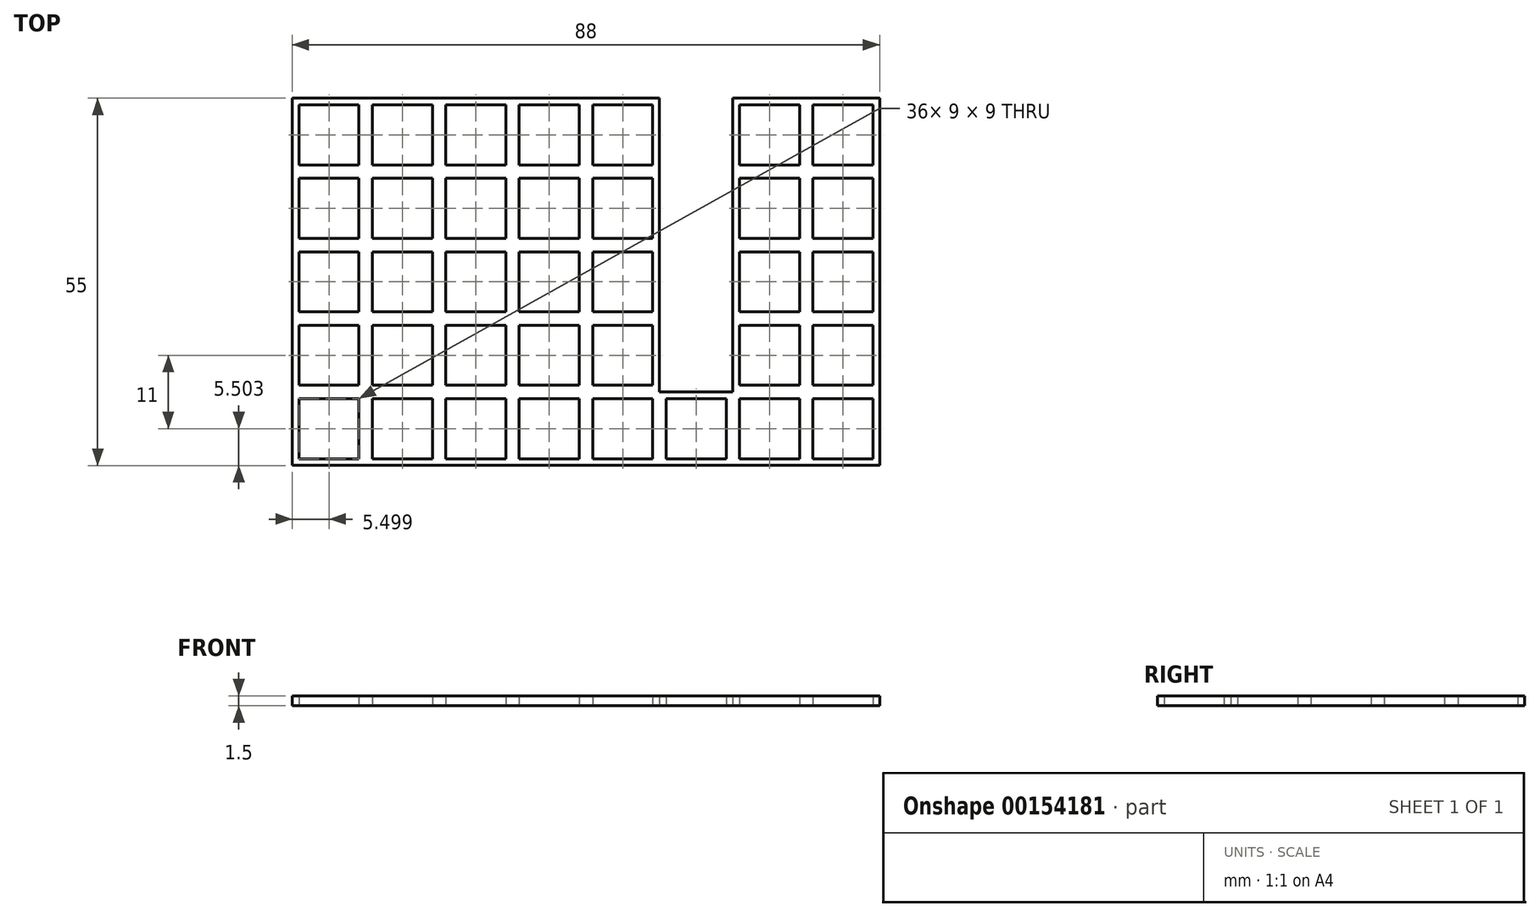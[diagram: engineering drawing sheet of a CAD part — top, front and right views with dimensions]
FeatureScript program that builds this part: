
annotation { "Feature Type Name" : "Feature", "Feature Type Description" : "" }
export const myFeature = defineFeature(function(context is Context, id is Id, definition is map)
    precondition{}
    {
        {
            var Q0;
            Q0=qCreatedBy(makeId("Top.planeOp"),FACE);
            var sketch = newSketch(context, id + "F0", { "sketchPlane" : qUnion([Q0])});
            skLineSegment(sketch, "E0.bottom", {"start": v(-68.25, 31) * mm, "end": v(19.75, 31) * mm, "construction": true});
            skLineSegment(sketch, "E0.top", {"start": v(-68.25, -24) * mm, "end": v(19.75, -24) * mm, "construction": true});
            skLineSegment(sketch, "E0.left", {"start": v(-68.25, 31) * mm, "end": v(-68.25, -24) * mm, "construction": true});
            skLineSegment(sketch, "E0.right", {"start": v(19.75, 31) * mm, "end": v(19.75, -24) * mm, "construction": true});
            skLineSegment(sketch, "E1.bottom", {"start": v(-68.25, -24) * mm, "end": v(-57.25, -24) * mm, "construction": true});
            skLineSegment(sketch, "E1.top", {"start": v(-68.25, -13) * mm, "end": v(-57.25, -13) * mm, "construction": true});
            skLineSegment(sketch, "E1.right", {"start": v(-57.25, -24) * mm, "end": v(-57.25, -13) * mm, "construction": true});
            skLineSegment(sketch, "E2.bottom", {"start": v(-68.25, -13) * mm, "end": v(-57.25, -13) * mm});
            skLineSegment(sketch, "E2.top", {"start": v(-68.25, -24) * mm, "end": v(-57.25, -24) * mm});
            skLineSegment(sketch, "E2.left", {"start": v(-68.25, -13) * mm, "end": v(-68.25, -24) * mm});
            skLineSegment(sketch, "E2.right", {"start": v(-57.25, -13) * mm, "end": v(-57.25, -24) * mm});
            skLineSegment(sketch, "E3", {"start": v(-67.25, -14) * mm, "end": v(-58.25, -14) * mm});
            skLineSegment(sketch, "E4", {"start": v(-58.25, -14) * mm, "end": v(-58.25, -23) * mm});
            skLineSegment(sketch, "E5", {"start": v(-58.25, -23) * mm, "end": v(-67.25, -23) * mm});
            skLineSegment(sketch, "E6", {"start": v(-67.25, -23) * mm, "end": v(-67.25, -14) * mm});
            skLineSegment(sketch, "E7.1.0.0", {"start": v(-47.25, -14) * mm, "end": v(-47.25, -23) * mm});
            skLineSegment(sketch, "E7.1.0.1", {"start": v(-57.25, -24) * mm, "end": v(-46.25, -24) * mm});
            skLineSegment(sketch, "E7.1.0.2", {"start": v(-56.25, -23) * mm, "end": v(-56.25, -14) * mm});
            skLineSegment(sketch, "E7.1.0.3", {"start": v(-56.25, -14) * mm, "end": v(-47.25, -14) * mm});
            skLineSegment(sketch, "E7.1.0.4", {"start": v(-46.25, -13) * mm, "end": v(-46.25, -24) * mm});
            skLineSegment(sketch, "E7.1.0.6", {"start": v(-57.25, -13) * mm, "end": v(-46.25, -13) * mm});
            skLineSegment(sketch, "E7.1.0.7", {"start": v(-47.25, -23) * mm, "end": v(-56.25, -23) * mm});
            skLineSegment(sketch, "E7.1.0.8", {"start": v(-57.25, -24) * mm, "end": v(-46.25, -24) * mm, "construction": true});
            skLineSegment(sketch, "E7.1.0.9", {"start": v(-46.25, -24) * mm, "end": v(-46.25, -13) * mm, "construction": true});
            skLineSegment(sketch, "E7.1.0.10", {"start": v(-57.25, -13) * mm, "end": v(-46.25, -13) * mm, "construction": true});
            skLineSegment(sketch, "E7.2.0.0", {"start": v(-36.25, -14) * mm, "end": v(-36.25, -23) * mm});
            skLineSegment(sketch, "E7.2.0.1", {"start": v(-46.25, -24) * mm, "end": v(-35.25, -24) * mm});
            skLineSegment(sketch, "E7.2.0.2", {"start": v(-45.25, -23) * mm, "end": v(-45.25, -14) * mm});
            skLineSegment(sketch, "E7.2.0.3", {"start": v(-45.25, -14) * mm, "end": v(-36.25, -14) * mm});
            skLineSegment(sketch, "E7.2.0.4", {"start": v(-35.25, -13) * mm, "end": v(-35.25, -24) * mm});
            skLineSegment(sketch, "E7.2.0.5", {"start": v(-46.25, -13) * mm, "end": v(-46.25, -24) * mm});
            skLineSegment(sketch, "E7.2.0.6", {"start": v(-46.25, -13) * mm, "end": v(-35.25, -13) * mm});
            skLineSegment(sketch, "E7.2.0.7", {"start": v(-36.25, -23) * mm, "end": v(-45.25, -23) * mm});
            skLineSegment(sketch, "E7.2.0.8", {"start": v(-46.25, -24) * mm, "end": v(-35.25, -24) * mm, "construction": true});
            skLineSegment(sketch, "E7.2.0.9", {"start": v(-35.25, -24) * mm, "end": v(-35.25, -13) * mm, "construction": true});
            skLineSegment(sketch, "E7.2.0.10", {"start": v(-46.25, -13) * mm, "end": v(-35.25, -13) * mm, "construction": true});
            skLineSegment(sketch, "E7.3.0.0", {"start": v(-25.25, -14) * mm, "end": v(-25.25, -23) * mm});
            skLineSegment(sketch, "E7.3.0.1", {"start": v(-35.25, -24) * mm, "end": v(-24.25, -24) * mm});
            skLineSegment(sketch, "E7.3.0.2", {"start": v(-34.25, -23) * mm, "end": v(-34.25, -14) * mm});
            skLineSegment(sketch, "E7.3.0.3", {"start": v(-34.25, -14) * mm, "end": v(-25.25, -14) * mm});
            skLineSegment(sketch, "E7.3.0.4", {"start": v(-24.25, -13) * mm, "end": v(-24.25, -24) * mm});
            skLineSegment(sketch, "E7.3.0.5", {"start": v(-35.25, -13) * mm, "end": v(-35.25, -24) * mm});
            skLineSegment(sketch, "E7.3.0.6", {"start": v(-35.25, -13) * mm, "end": v(-24.25, -13) * mm});
            skLineSegment(sketch, "E7.3.0.7", {"start": v(-25.25, -23) * mm, "end": v(-34.25, -23) * mm});
            skLineSegment(sketch, "E7.3.0.8", {"start": v(-35.25, -24) * mm, "end": v(-24.25, -24) * mm, "construction": true});
            skLineSegment(sketch, "E7.3.0.9", {"start": v(-24.25, -24) * mm, "end": v(-24.25, -13) * mm, "construction": true});
            skLineSegment(sketch, "E7.3.0.10", {"start": v(-35.25, -13) * mm, "end": v(-24.25, -13) * mm, "construction": true});
            skLineSegment(sketch, "E7.4.0.0", {"start": v(-14.25, -14) * mm, "end": v(-14.25, -23) * mm});
            skLineSegment(sketch, "E7.4.0.1", {"start": v(-24.25, -24) * mm, "end": v(-13.25, -24) * mm});
            skLineSegment(sketch, "E7.4.0.2", {"start": v(-23.25, -23) * mm, "end": v(-23.25, -14) * mm});
            skLineSegment(sketch, "E7.4.0.3", {"start": v(-23.25, -14) * mm, "end": v(-14.25, -14) * mm});
            skLineSegment(sketch, "E7.4.0.4", {"start": v(-13.25, -13) * mm, "end": v(-13.25, -24) * mm});
            skLineSegment(sketch, "E7.4.0.5", {"start": v(-24.25, -13) * mm, "end": v(-24.25, -24) * mm});
            skLineSegment(sketch, "E7.4.0.6", {"start": v(-24.25, -13) * mm, "end": v(-13.25, -13) * mm});
            skLineSegment(sketch, "E7.4.0.7", {"start": v(-14.25, -23) * mm, "end": v(-23.25, -23) * mm});
            skLineSegment(sketch, "E7.4.0.8", {"start": v(-24.25, -24) * mm, "end": v(-13.25, -24) * mm, "construction": true});
            skLineSegment(sketch, "E7.4.0.9", {"start": v(-13.25, -24) * mm, "end": v(-13.25, -13) * mm, "construction": true});
            skLineSegment(sketch, "E7.4.0.10", {"start": v(-24.25, -13) * mm, "end": v(-13.25, -13) * mm, "construction": true});
            skLineSegment(sketch, "E7.5.0.0", {"start": v(-3.25, -14) * mm, "end": v(-3.25, -23) * mm});
            skLineSegment(sketch, "E7.5.0.1", {"start": v(-13.25, -24) * mm, "end": v(-2.25, -24) * mm});
            skLineSegment(sketch, "E7.5.0.2", {"start": v(-12.25, -23) * mm, "end": v(-12.25, -14) * mm});
            skLineSegment(sketch, "E7.5.0.3", {"start": v(-12.25, -14) * mm, "end": v(-3.25, -14) * mm});
            skLineSegment(sketch, "E7.5.0.4", {"start": v(-2.25, -13) * mm, "end": v(-2.25, -24) * mm});
            skLineSegment(sketch, "E7.5.0.5", {"start": v(-13.25, -13) * mm, "end": v(-13.25, -24) * mm});
            skLineSegment(sketch, "E7.5.0.6", {"start": v(-13.25, -13) * mm, "end": v(-2.25, -13) * mm});
            skLineSegment(sketch, "E7.5.0.7", {"start": v(-3.25, -23) * mm, "end": v(-12.25, -23) * mm});
            skLineSegment(sketch, "E7.5.0.8", {"start": v(-13.25, -24) * mm, "end": v(-2.25, -24) * mm, "construction": true});
            skLineSegment(sketch, "E7.5.0.9", {"start": v(-2.25, -24) * mm, "end": v(-2.25, -13) * mm, "construction": true});
            skLineSegment(sketch, "E7.5.0.10", {"start": v(-13.25, -13) * mm, "end": v(-2.25, -13) * mm, "construction": true});
            skLineSegment(sketch, "E7.6.0.0", {"start": v(7.75, -14) * mm, "end": v(7.75, -23) * mm});
            skLineSegment(sketch, "E7.6.0.1", {"start": v(-2.25, -24) * mm, "end": v(8.75, -24) * mm});
            skLineSegment(sketch, "E7.6.0.2", {"start": v(-1.25, -23) * mm, "end": v(-1.25, -14) * mm});
            skLineSegment(sketch, "E7.6.0.3", {"start": v(-1.25, -14) * mm, "end": v(7.75, -14) * mm});
            skLineSegment(sketch, "E7.6.0.4", {"start": v(8.75, -13) * mm, "end": v(8.75, -24) * mm});
            skLineSegment(sketch, "E7.6.0.5", {"start": v(-2.25, -13) * mm, "end": v(-2.25, -24) * mm});
            skLineSegment(sketch, "E7.6.0.6", {"start": v(-2.25, -13) * mm, "end": v(8.75, -13) * mm});
            skLineSegment(sketch, "E7.6.0.7", {"start": v(7.75, -23) * mm, "end": v(-1.25, -23) * mm});
            skLineSegment(sketch, "E7.6.0.8", {"start": v(-2.25, -24) * mm, "end": v(8.75, -24) * mm, "construction": true});
            skLineSegment(sketch, "E7.6.0.9", {"start": v(8.75, -24) * mm, "end": v(8.75, -13) * mm, "construction": true});
            skLineSegment(sketch, "E7.6.0.10", {"start": v(-2.25, -13) * mm, "end": v(8.75, -13) * mm, "construction": true});
            skLineSegment(sketch, "E7.7.0.0", {"start": v(18.75, -14) * mm, "end": v(18.75, -23) * mm});
            skLineSegment(sketch, "E7.7.0.1", {"start": v(8.75, -24) * mm, "end": v(19.75, -24) * mm});
            skLineSegment(sketch, "E7.7.0.2", {"start": v(9.75, -23) * mm, "end": v(9.75, -14) * mm});
            skLineSegment(sketch, "E7.7.0.3", {"start": v(9.75, -14) * mm, "end": v(18.75, -14) * mm});
            skLineSegment(sketch, "E7.7.0.4", {"start": v(19.75, -13) * mm, "end": v(19.75, -24) * mm});
            skLineSegment(sketch, "E7.7.0.5", {"start": v(8.75, -13) * mm, "end": v(8.75, -24) * mm});
            skLineSegment(sketch, "E7.7.0.6", {"start": v(8.75, -13) * mm, "end": v(19.75, -13) * mm});
            skLineSegment(sketch, "E7.7.0.7", {"start": v(18.75, -23) * mm, "end": v(9.75, -23) * mm});
            skLineSegment(sketch, "E7.7.0.8", {"start": v(8.75, -24) * mm, "end": v(19.75, -24) * mm, "construction": true});
            skLineSegment(sketch, "E7.7.0.9", {"start": v(19.75, -24) * mm, "end": v(19.75, -13) * mm, "construction": true});
            skLineSegment(sketch, "E7.7.0.10", {"start": v(8.75, -13) * mm, "end": v(19.75, -13) * mm, "construction": true});
            skLineSegment(sketch, "E8.0.1.0", {"start": v(-56.25, -12) * mm, "end": v(-56.25, -3) * mm});
            skLineSegment(sketch, "E8.0.1.1", {"start": v(-46.25, -2) * mm, "end": v(-35.25, -2) * mm});
            skLineSegment(sketch, "E8.0.1.2", {"start": v(-14.25, -3) * mm, "end": v(-14.25, -12) * mm});
            skLineSegment(sketch, "E8.0.1.3", {"start": v(-13.25, -2) * mm, "end": v(-13.25, -13) * mm});
            skLineSegment(sketch, "E8.0.1.5", {"start": v(-2.25, -2) * mm, "end": v(8.75, -2) * mm});
            skLineSegment(sketch, "E8.0.1.6", {"start": v(-45.25, -12) * mm, "end": v(-45.25, -3) * mm});
            skLineSegment(sketch, "E8.0.1.7", {"start": v(-25.25, -12) * mm, "end": v(-34.25, -12) * mm});
            skLineSegment(sketch, "E8.0.1.9", {"start": v(-45.25, -3) * mm, "end": v(-36.25, -3) * mm});
            skLineSegment(sketch, "E8.0.1.10", {"start": v(-58.25, -3) * mm, "end": v(-58.25, -12) * mm});
            skLineSegment(sketch, "E8.0.1.11", {"start": v(-12.25, -12) * mm, "end": v(-12.25, -3) * mm});
            skLineSegment(sketch, "E8.0.1.12", {"start": v(-67.25, -3) * mm, "end": v(-58.25, -3) * mm});
            skLineSegment(sketch, "E8.0.1.13", {"start": v(-57.25, -2) * mm, "end": v(-57.25, -13) * mm});
            skLineSegment(sketch, "E8.0.1.14", {"start": v(-68.25, -2) * mm, "end": v(-68.25, -13) * mm});
            skLineSegment(sketch, "E8.0.1.16", {"start": v(7.75, -12) * mm, "end": v(-1.25, -12) * mm});
            skLineSegment(sketch, "E8.0.1.18", {"start": v(-35.25, -2) * mm, "end": v(-24.25, -2) * mm});
            skLineSegment(sketch, "E8.0.1.19", {"start": v(-3.25, -3) * mm, "end": v(-3.25, -12) * mm});
            skLineSegment(sketch, "E8.0.1.20", {"start": v(8.75, -2) * mm, "end": v(8.75, -13) * mm});
            skLineSegment(sketch, "E8.0.1.21", {"start": v(-36.25, -3) * mm, "end": v(-36.25, -12) * mm});
            skLineSegment(sketch, "E8.0.1.22", {"start": v(-68.25, -2) * mm, "end": v(-57.25, -2) * mm});
            skLineSegment(sketch, "E8.0.1.23", {"start": v(-47.25, -3) * mm, "end": v(-47.25, -12) * mm});
            skLineSegment(sketch, "E8.0.1.24", {"start": v(-67.25, -12) * mm, "end": v(-67.25, -3) * mm});
            skLineSegment(sketch, "E8.0.1.25", {"start": v(-58.25, -12) * mm, "end": v(-67.25, -12) * mm});
            skLineSegment(sketch, "E8.0.1.26", {"start": v(-46.25, -2) * mm, "end": v(-46.25, -13) * mm});
            skLineSegment(sketch, "E8.0.1.27", {"start": v(-2.25, -2) * mm, "end": v(-2.25, -13) * mm});
            skLineSegment(sketch, "E8.0.1.28", {"start": v(-1.25, -3) * mm, "end": v(7.75, -3) * mm});
            skLineSegment(sketch, "E8.0.1.29", {"start": v(-24.25, -2) * mm, "end": v(-24.25, -13) * mm});
            skLineSegment(sketch, "E8.0.1.30", {"start": v(-35.25, -2) * mm, "end": v(-35.25, -13) * mm});
            skLineSegment(sketch, "E8.0.1.31", {"start": v(-12.25, -3) * mm, "end": v(-3.25, -3) * mm});
            skLineSegment(sketch, "E8.0.1.32", {"start": v(-1.25, -12) * mm, "end": v(-1.25, -3) * mm});
            skLineSegment(sketch, "E8.0.1.33", {"start": v(18.75, -12) * mm, "end": v(9.75, -12) * mm});
            skLineSegment(sketch, "E8.0.1.34", {"start": v(-34.25, -3) * mm, "end": v(-25.25, -3) * mm});
            skLineSegment(sketch, "E8.0.1.35", {"start": v(18.75, -3) * mm, "end": v(18.75, -12) * mm});
            skLineSegment(sketch, "E8.0.1.36", {"start": v(-13.25, -2) * mm, "end": v(-2.25, -2) * mm});
            skLineSegment(sketch, "E8.0.1.38", {"start": v(-36.25, -12) * mm, "end": v(-45.25, -12) * mm});
            skLineSegment(sketch, "E8.0.1.40", {"start": v(8.75, -2) * mm, "end": v(19.75, -2) * mm});
            skLineSegment(sketch, "E8.0.1.41", {"start": v(-56.25, -3) * mm, "end": v(-47.25, -3) * mm});
            skLineSegment(sketch, "E8.0.1.43", {"start": v(-34.25, -12) * mm, "end": v(-34.25, -3) * mm});
            skLineSegment(sketch, "E8.0.1.44", {"start": v(-14.25, -12) * mm, "end": v(-23.25, -12) * mm});
            skLineSegment(sketch, "E8.0.1.45", {"start": v(-57.25, -2) * mm, "end": v(-46.25, -2) * mm});
            skLineSegment(sketch, "E8.0.1.46", {"start": v(19.75, -2) * mm, "end": v(19.75, -13) * mm});
            skLineSegment(sketch, "E8.0.1.47", {"start": v(-25.25, -3) * mm, "end": v(-25.25, -12) * mm});
            skLineSegment(sketch, "E8.0.1.48", {"start": v(-47.25, -12) * mm, "end": v(-56.25, -12) * mm});
            skLineSegment(sketch, "E8.0.1.49", {"start": v(7.75, -3) * mm, "end": v(7.75, -12) * mm});
            skLineSegment(sketch, "E8.0.1.50", {"start": v(-24.25, -2) * mm, "end": v(-13.25, -2) * mm});
            skLineSegment(sketch, "E8.0.1.52", {"start": v(-23.25, -12) * mm, "end": v(-23.25, -3) * mm});
            skLineSegment(sketch, "E8.0.1.53", {"start": v(-3.25, -12) * mm, "end": v(-12.25, -12) * mm});
            skLineSegment(sketch, "E8.0.1.54", {"start": v(9.75, -12) * mm, "end": v(9.75, -3) * mm});
            skLineSegment(sketch, "E8.0.1.55", {"start": v(9.75, -3) * mm, "end": v(18.75, -3) * mm});
            skLineSegment(sketch, "E8.0.1.56", {"start": v(-23.25, -3) * mm, "end": v(-14.25, -3) * mm});
            skLineSegment(sketch, "E8.0.1.57", {"start": v(-2.25, -2) * mm, "end": v(8.75, -2) * mm, "construction": true});
            skLineSegment(sketch, "E8.0.1.58", {"start": v(-2.25, -2) * mm, "end": v(-2.25, -13) * mm});
            skLineSegment(sketch, "E8.0.1.59", {"start": v(8.75, -2) * mm, "end": v(19.75, -2) * mm, "construction": true});
            skLineSegment(sketch, "E8.0.1.60", {"start": v(19.75, -13) * mm, "end": v(19.75, -2) * mm, "construction": true});
            skLineSegment(sketch, "E8.0.1.61", {"start": v(-35.25, -2) * mm, "end": v(-35.25, -13) * mm});
            skLineSegment(sketch, "E8.0.1.62", {"start": v(-24.25, -2) * mm, "end": v(-13.25, -2) * mm, "construction": true});
            skLineSegment(sketch, "E8.0.1.63", {"start": v(-68.25, -2) * mm, "end": v(-57.25, -2) * mm, "construction": true});
            skLineSegment(sketch, "E8.0.1.65", {"start": v(-68.25, -13) * mm, "end": v(19.75, -13) * mm, "construction": true});
            skLineSegment(sketch, "E8.0.1.66", {"start": v(-35.25, -2) * mm, "end": v(-24.25, -2) * mm, "construction": true});
            skLineSegment(sketch, "E8.0.1.67", {"start": v(-57.25, -2) * mm, "end": v(-46.25, -2) * mm, "construction": true});
            skLineSegment(sketch, "E8.0.1.68", {"start": v(-13.25, -2) * mm, "end": v(-13.25, -13) * mm});
            skLineSegment(sketch, "E8.0.1.69", {"start": v(-46.25, -2) * mm, "end": v(-35.25, -2) * mm, "construction": true});
            skLineSegment(sketch, "E8.0.1.70", {"start": v(-13.25, -2) * mm, "end": v(-2.25, -2) * mm, "construction": true});
            skLineSegment(sketch, "E8.0.1.71", {"start": v(-24.25, -2) * mm, "end": v(-24.25, -13) * mm});
            skLineSegment(sketch, "E8.0.1.72", {"start": v(8.75, -2) * mm, "end": v(8.75, -13) * mm});
            skLineSegment(sketch, "E8.0.1.74", {"start": v(-46.25, -2) * mm, "end": v(-46.25, -13) * mm});
            skLineSegment(sketch, "E8.0.1.75", {"start": v(-57.25, -2) * mm, "end": v(-57.25, -13) * mm});
            skLineSegment(sketch, "E8.0.1.79", {"start": v(-57.25, -13) * mm, "end": v(-57.25, -2) * mm, "construction": true});
            skLineSegment(sketch, "E8.0.1.80", {"start": v(8.75, -13) * mm, "end": v(8.75, -2) * mm, "construction": true});
            skLineSegment(sketch, "E8.0.1.82", {"start": v(-13.25, -13) * mm, "end": v(-13.25, -2) * mm, "construction": true});
            skLineSegment(sketch, "E8.0.1.83", {"start": v(-24.25, -13) * mm, "end": v(-24.25, -2) * mm, "construction": true});
            skLineSegment(sketch, "E8.0.1.84", {"start": v(-46.25, -13) * mm, "end": v(-46.25, -2) * mm, "construction": true});
            skLineSegment(sketch, "E8.0.1.88", {"start": v(-2.25, -13) * mm, "end": v(-2.25, -2) * mm, "construction": true});
            skLineSegment(sketch, "E8.0.1.89", {"start": v(-35.25, -13) * mm, "end": v(-35.25, -2) * mm, "construction": true});
            skLineSegment(sketch, "E8.0.2.0", {"start": v(-56.25, -1) * mm, "end": v(-56.25, 8) * mm});
            skLineSegment(sketch, "E8.0.2.1", {"start": v(-46.25, 9) * mm, "end": v(-35.25, 9) * mm});
            skLineSegment(sketch, "E8.0.2.2", {"start": v(-14.25, 8) * mm, "end": v(-14.25, -1) * mm});
            skLineSegment(sketch, "E8.0.2.3", {"start": v(-13.25, 9) * mm, "end": v(-13.25, -2) * mm});
            skLineSegment(sketch, "E8.0.2.4", {"start": v(-57.25, -2) * mm, "end": v(-46.25, -2) * mm});
            skLineSegment(sketch, "E8.0.2.5", {"start": v(-2.25, 9) * mm, "end": v(8.75, 9) * mm});
            skLineSegment(sketch, "E8.0.2.6", {"start": v(-45.25, -1) * mm, "end": v(-45.25, 8) * mm});
            skLineSegment(sketch, "E8.0.2.7", {"start": v(-25.25, -1) * mm, "end": v(-34.25, -1) * mm});
            skLineSegment(sketch, "E8.0.2.8", {"start": v(-13.25, -2) * mm, "end": v(-2.25, -2) * mm});
            skLineSegment(sketch, "E8.0.2.9", {"start": v(-45.25, 8) * mm, "end": v(-36.25, 8) * mm});
            skLineSegment(sketch, "E8.0.2.10", {"start": v(-58.25, 8) * mm, "end": v(-58.25, -1) * mm});
            skLineSegment(sketch, "E8.0.2.11", {"start": v(-12.25, -1) * mm, "end": v(-12.25, 8) * mm});
            skLineSegment(sketch, "E8.0.2.12", {"start": v(-67.25, 8) * mm, "end": v(-58.25, 8) * mm});
            skLineSegment(sketch, "E8.0.2.13", {"start": v(-57.25, 9) * mm, "end": v(-57.25, -2) * mm});
            skLineSegment(sketch, "E8.0.2.14", {"start": v(-68.25, 9) * mm, "end": v(-68.25, -2) * mm});
            skLineSegment(sketch, "E8.0.2.15", {"start": v(-68.25, -2) * mm, "end": v(-57.25, -2) * mm});
            skLineSegment(sketch, "E8.0.2.16", {"start": v(7.75, -1) * mm, "end": v(-1.25, -1) * mm});
            skLineSegment(sketch, "E8.0.2.17", {"start": v(-46.25, -2) * mm, "end": v(-35.25, -2) * mm});
            skLineSegment(sketch, "E8.0.2.18", {"start": v(-35.25, 9) * mm, "end": v(-24.25, 9) * mm});
            skLineSegment(sketch, "E8.0.2.19", {"start": v(-3.25, 8) * mm, "end": v(-3.25, -1) * mm});
            skLineSegment(sketch, "E8.0.2.20", {"start": v(8.75, 9) * mm, "end": v(8.75, -2) * mm});
            skLineSegment(sketch, "E8.0.2.21", {"start": v(-36.25, 8) * mm, "end": v(-36.25, -1) * mm});
            skLineSegment(sketch, "E8.0.2.22", {"start": v(-68.25, 9) * mm, "end": v(-57.25, 9) * mm});
            skLineSegment(sketch, "E8.0.2.23", {"start": v(-47.25, 8) * mm, "end": v(-47.25, -1) * mm});
            skLineSegment(sketch, "E8.0.2.24", {"start": v(-67.25, -1) * mm, "end": v(-67.25, 8) * mm});
            skLineSegment(sketch, "E8.0.2.25", {"start": v(-58.25, -1) * mm, "end": v(-67.25, -1) * mm});
            skLineSegment(sketch, "E8.0.2.26", {"start": v(-46.25, 9) * mm, "end": v(-46.25, -2) * mm});
            skLineSegment(sketch, "E8.0.2.27", {"start": v(-2.25, 9) * mm, "end": v(-2.25, -2) * mm});
            skLineSegment(sketch, "E8.0.2.28", {"start": v(-1.25, 8) * mm, "end": v(7.75, 8) * mm});
            skLineSegment(sketch, "E8.0.2.29", {"start": v(-24.25, 9) * mm, "end": v(-24.25, -2) * mm});
            skLineSegment(sketch, "E8.0.2.30", {"start": v(-35.25, 9) * mm, "end": v(-35.25, -2) * mm});
            skLineSegment(sketch, "E8.0.2.31", {"start": v(-12.25, 8) * mm, "end": v(-3.25, 8) * mm});
            skLineSegment(sketch, "E8.0.2.32", {"start": v(-1.25, -1) * mm, "end": v(-1.25, 8) * mm});
            skLineSegment(sketch, "E8.0.2.33", {"start": v(18.75, -1) * mm, "end": v(9.75, -1) * mm});
            skLineSegment(sketch, "E8.0.2.34", {"start": v(-34.25, 8) * mm, "end": v(-25.25, 8) * mm});
            skLineSegment(sketch, "E8.0.2.35", {"start": v(18.75, 8) * mm, "end": v(18.75, -1) * mm});
            skLineSegment(sketch, "E8.0.2.36", {"start": v(-13.25, 9) * mm, "end": v(-2.25, 9) * mm});
            skLineSegment(sketch, "E8.0.2.37", {"start": v(-24.25, -2) * mm, "end": v(-13.25, -2) * mm});
            skLineSegment(sketch, "E8.0.2.38", {"start": v(-36.25, -1) * mm, "end": v(-45.25, -1) * mm});
            skLineSegment(sketch, "E8.0.2.39", {"start": v(-2.25, -2) * mm, "end": v(8.75, -2) * mm});
            skLineSegment(sketch, "E8.0.2.40", {"start": v(8.75, 9) * mm, "end": v(19.75, 9) * mm});
            skLineSegment(sketch, "E8.0.2.41", {"start": v(-56.25, 8) * mm, "end": v(-47.25, 8) * mm});
            skLineSegment(sketch, "E8.0.2.42", {"start": v(8.75, -2) * mm, "end": v(19.75, -2) * mm});
            skLineSegment(sketch, "E8.0.2.43", {"start": v(-34.25, -1) * mm, "end": v(-34.25, 8) * mm});
            skLineSegment(sketch, "E8.0.2.44", {"start": v(-14.25, -1) * mm, "end": v(-23.25, -1) * mm});
            skLineSegment(sketch, "E8.0.2.45", {"start": v(-57.25, 9) * mm, "end": v(-46.25, 9) * mm});
            skLineSegment(sketch, "E8.0.2.46", {"start": v(19.75, 9) * mm, "end": v(19.75, -2) * mm});
            skLineSegment(sketch, "E8.0.2.47", {"start": v(-25.25, 8) * mm, "end": v(-25.25, -1) * mm});
            skLineSegment(sketch, "E8.0.2.48", {"start": v(-47.25, -1) * mm, "end": v(-56.25, -1) * mm});
            skLineSegment(sketch, "E8.0.2.49", {"start": v(7.75, 8) * mm, "end": v(7.75, -1) * mm});
            skLineSegment(sketch, "E8.0.2.50", {"start": v(-24.25, 9) * mm, "end": v(-13.25, 9) * mm});
            skLineSegment(sketch, "E8.0.2.51", {"start": v(-35.25, -2) * mm, "end": v(-24.25, -2) * mm});
            skLineSegment(sketch, "E8.0.2.52", {"start": v(-23.25, -1) * mm, "end": v(-23.25, 8) * mm});
            skLineSegment(sketch, "E8.0.2.53", {"start": v(-3.25, -1) * mm, "end": v(-12.25, -1) * mm});
            skLineSegment(sketch, "E8.0.2.54", {"start": v(9.75, -1) * mm, "end": v(9.75, 8) * mm});
            skLineSegment(sketch, "E8.0.2.55", {"start": v(9.75, 8) * mm, "end": v(18.75, 8) * mm});
            skLineSegment(sketch, "E8.0.2.56", {"start": v(-23.25, 8) * mm, "end": v(-14.25, 8) * mm});
            skLineSegment(sketch, "E8.0.2.57", {"start": v(-2.25, 9) * mm, "end": v(8.75, 9) * mm, "construction": true});
            skLineSegment(sketch, "E8.0.2.58", {"start": v(-2.25, 9) * mm, "end": v(-2.25, -2) * mm});
            skLineSegment(sketch, "E8.0.2.59", {"start": v(8.75, 9) * mm, "end": v(19.75, 9) * mm, "construction": true});
            skLineSegment(sketch, "E8.0.2.60", {"start": v(19.75, -2) * mm, "end": v(19.75, 9) * mm, "construction": true});
            skLineSegment(sketch, "E8.0.2.61", {"start": v(-35.25, 9) * mm, "end": v(-35.25, -2) * mm});
            skLineSegment(sketch, "E8.0.2.62", {"start": v(-24.25, 9) * mm, "end": v(-13.25, 9) * mm, "construction": true});
            skLineSegment(sketch, "E8.0.2.63", {"start": v(-68.25, 9) * mm, "end": v(-57.25, 9) * mm, "construction": true});
            skLineSegment(sketch, "E8.0.2.64", {"start": v(-68.25, -2) * mm, "end": v(-57.25, -2) * mm, "construction": true});
            skLineSegment(sketch, "E8.0.2.65", {"start": v(-68.25, -2) * mm, "end": v(19.75, -2) * mm, "construction": true});
            skLineSegment(sketch, "E8.0.2.66", {"start": v(-35.25, 9) * mm, "end": v(-24.25, 9) * mm, "construction": true});
            skLineSegment(sketch, "E8.0.2.67", {"start": v(-57.25, 9) * mm, "end": v(-46.25, 9) * mm, "construction": true});
            skLineSegment(sketch, "E8.0.2.68", {"start": v(-13.25, 9) * mm, "end": v(-13.25, -2) * mm});
            skLineSegment(sketch, "E8.0.2.69", {"start": v(-46.25, 9) * mm, "end": v(-35.25, 9) * mm, "construction": true});
            skLineSegment(sketch, "E8.0.2.70", {"start": v(-13.25, 9) * mm, "end": v(-2.25, 9) * mm, "construction": true});
            skLineSegment(sketch, "E8.0.2.71", {"start": v(-24.25, 9) * mm, "end": v(-24.25, -2) * mm});
            skLineSegment(sketch, "E8.0.2.72", {"start": v(8.75, 9) * mm, "end": v(8.75, -2) * mm});
            skLineSegment(sketch, "E8.0.2.73", {"start": v(-46.25, -2) * mm, "end": v(-35.25, -2) * mm, "construction": true});
            skLineSegment(sketch, "E8.0.2.74", {"start": v(-46.25, 9) * mm, "end": v(-46.25, -2) * mm});
            skLineSegment(sketch, "E8.0.2.75", {"start": v(-57.25, 9) * mm, "end": v(-57.25, -2) * mm});
            skLineSegment(sketch, "E8.0.2.76", {"start": v(-2.25, -2) * mm, "end": v(8.75, -2) * mm, "construction": true});
            skLineSegment(sketch, "E8.0.2.77", {"start": v(-68.25, -2) * mm, "end": v(-57.25, -2) * mm, "construction": true});
            skLineSegment(sketch, "E8.0.2.78", {"start": v(-35.25, -2) * mm, "end": v(-24.25, -2) * mm, "construction": true});
            skLineSegment(sketch, "E8.0.2.79", {"start": v(-57.25, -2) * mm, "end": v(-57.25, 9) * mm, "construction": true});
            skLineSegment(sketch, "E8.0.2.80", {"start": v(8.75, -2) * mm, "end": v(8.75, 9) * mm, "construction": true});
            skLineSegment(sketch, "E8.0.2.81", {"start": v(8.75, -2) * mm, "end": v(19.75, -2) * mm, "construction": true});
            skLineSegment(sketch, "E8.0.2.82", {"start": v(-13.25, -2) * mm, "end": v(-13.25, 9) * mm, "construction": true});
            skLineSegment(sketch, "E8.0.2.83", {"start": v(-24.25, -2) * mm, "end": v(-24.25, 9) * mm, "construction": true});
            skLineSegment(sketch, "E8.0.2.84", {"start": v(-46.25, -2) * mm, "end": v(-46.25, 9) * mm, "construction": true});
            skLineSegment(sketch, "E8.0.2.85", {"start": v(-24.25, -2) * mm, "end": v(-13.25, -2) * mm, "construction": true});
            skLineSegment(sketch, "E8.0.2.86", {"start": v(-57.25, -2) * mm, "end": v(-46.25, -2) * mm, "construction": true});
            skLineSegment(sketch, "E8.0.2.87", {"start": v(-13.25, -2) * mm, "end": v(-2.25, -2) * mm, "construction": true});
            skLineSegment(sketch, "E8.0.2.88", {"start": v(-2.25, -2) * mm, "end": v(-2.25, 9) * mm, "construction": true});
            skLineSegment(sketch, "E8.0.2.89", {"start": v(-35.25, -2) * mm, "end": v(-35.25, 9) * mm, "construction": true});
            skLineSegment(sketch, "E8.0.3.0", {"start": v(-56.25, 10) * mm, "end": v(-56.25, 19) * mm});
            skLineSegment(sketch, "E8.0.3.1", {"start": v(-46.25, 20) * mm, "end": v(-35.25, 20) * mm});
            skLineSegment(sketch, "E8.0.3.2", {"start": v(-14.25, 19) * mm, "end": v(-14.25, 10) * mm});
            skLineSegment(sketch, "E8.0.3.3", {"start": v(-13.25, 20) * mm, "end": v(-13.25, 9) * mm});
            skLineSegment(sketch, "E8.0.3.4", {"start": v(-57.25, 9) * mm, "end": v(-46.25, 9) * mm});
            skLineSegment(sketch, "E8.0.3.5", {"start": v(-2.25, 20) * mm, "end": v(8.75, 20) * mm});
            skLineSegment(sketch, "E8.0.3.6", {"start": v(-45.25, 10) * mm, "end": v(-45.25, 19) * mm});
            skLineSegment(sketch, "E8.0.3.7", {"start": v(-25.25, 10) * mm, "end": v(-34.25, 10) * mm});
            skLineSegment(sketch, "E8.0.3.8", {"start": v(-13.25, 9) * mm, "end": v(-2.25, 9) * mm});
            skLineSegment(sketch, "E8.0.3.9", {"start": v(-45.25, 19) * mm, "end": v(-36.25, 19) * mm});
            skLineSegment(sketch, "E8.0.3.10", {"start": v(-58.25, 19) * mm, "end": v(-58.25, 10) * mm});
            skLineSegment(sketch, "E8.0.3.11", {"start": v(-12.25, 10) * mm, "end": v(-12.25, 19) * mm});
            skLineSegment(sketch, "E8.0.3.12", {"start": v(-67.25, 19) * mm, "end": v(-58.25, 19) * mm});
            skLineSegment(sketch, "E8.0.3.13", {"start": v(-57.25, 20) * mm, "end": v(-57.25, 9) * mm});
            skLineSegment(sketch, "E8.0.3.14", {"start": v(-68.25, 20) * mm, "end": v(-68.25, 9) * mm});
            skLineSegment(sketch, "E8.0.3.15", {"start": v(-68.25, 9) * mm, "end": v(-57.25, 9) * mm});
            skLineSegment(sketch, "E8.0.3.16", {"start": v(7.75, 10) * mm, "end": v(-1.25, 10) * mm});
            skLineSegment(sketch, "E8.0.3.17", {"start": v(-46.25, 9) * mm, "end": v(-35.25, 9) * mm});
            skLineSegment(sketch, "E8.0.3.18", {"start": v(-35.25, 20) * mm, "end": v(-24.25, 20) * mm});
            skLineSegment(sketch, "E8.0.3.19", {"start": v(-3.25, 19) * mm, "end": v(-3.25, 10) * mm});
            skLineSegment(sketch, "E8.0.3.20", {"start": v(8.75, 20) * mm, "end": v(8.75, 9) * mm});
            skLineSegment(sketch, "E8.0.3.21", {"start": v(-36.25, 19) * mm, "end": v(-36.25, 10) * mm});
            skLineSegment(sketch, "E8.0.3.22", {"start": v(-68.25, 20) * mm, "end": v(-57.25, 20) * mm});
            skLineSegment(sketch, "E8.0.3.23", {"start": v(-47.25, 19) * mm, "end": v(-47.25, 10) * mm});
            skLineSegment(sketch, "E8.0.3.24", {"start": v(-67.25, 10) * mm, "end": v(-67.25, 19) * mm});
            skLineSegment(sketch, "E8.0.3.25", {"start": v(-58.25, 10) * mm, "end": v(-67.25, 10) * mm});
            skLineSegment(sketch, "E8.0.3.26", {"start": v(-46.25, 20) * mm, "end": v(-46.25, 9) * mm});
            skLineSegment(sketch, "E8.0.3.27", {"start": v(-2.25, 20) * mm, "end": v(-2.25, 9) * mm});
            skLineSegment(sketch, "E8.0.3.28", {"start": v(-1.25, 19) * mm, "end": v(7.75, 19) * mm});
            skLineSegment(sketch, "E8.0.3.29", {"start": v(-24.25, 20) * mm, "end": v(-24.25, 9) * mm});
            skLineSegment(sketch, "E8.0.3.30", {"start": v(-35.25, 20) * mm, "end": v(-35.25, 9) * mm});
            skLineSegment(sketch, "E8.0.3.31", {"start": v(-12.25, 19) * mm, "end": v(-3.25, 19) * mm});
            skLineSegment(sketch, "E8.0.3.32", {"start": v(-1.25, 10) * mm, "end": v(-1.25, 19) * mm});
            skLineSegment(sketch, "E8.0.3.33", {"start": v(18.75, 10) * mm, "end": v(9.75, 10) * mm});
            skLineSegment(sketch, "E8.0.3.34", {"start": v(-34.25, 19) * mm, "end": v(-25.25, 19) * mm});
            skLineSegment(sketch, "E8.0.3.35", {"start": v(18.75, 19) * mm, "end": v(18.75, 10) * mm});
            skLineSegment(sketch, "E8.0.3.36", {"start": v(-13.25, 20) * mm, "end": v(-2.25, 20) * mm});
            skLineSegment(sketch, "E8.0.3.37", {"start": v(-24.25, 9) * mm, "end": v(-13.25, 9) * mm});
            skLineSegment(sketch, "E8.0.3.38", {"start": v(-36.25, 10) * mm, "end": v(-45.25, 10) * mm});
            skLineSegment(sketch, "E8.0.3.39", {"start": v(-2.25, 9) * mm, "end": v(8.75, 9) * mm});
            skLineSegment(sketch, "E8.0.3.40", {"start": v(8.75, 20) * mm, "end": v(19.75, 20) * mm});
            skLineSegment(sketch, "E8.0.3.41", {"start": v(-56.25, 19) * mm, "end": v(-47.25, 19) * mm});
            skLineSegment(sketch, "E8.0.3.42", {"start": v(8.75, 9) * mm, "end": v(19.75, 9) * mm});
            skLineSegment(sketch, "E8.0.3.43", {"start": v(-34.25, 10) * mm, "end": v(-34.25, 19) * mm});
            skLineSegment(sketch, "E8.0.3.44", {"start": v(-14.25, 10) * mm, "end": v(-23.25, 10) * mm});
            skLineSegment(sketch, "E8.0.3.45", {"start": v(-57.25, 20) * mm, "end": v(-46.25, 20) * mm});
            skLineSegment(sketch, "E8.0.3.46", {"start": v(19.75, 20) * mm, "end": v(19.75, 9) * mm});
            skLineSegment(sketch, "E8.0.3.47", {"start": v(-25.25, 19) * mm, "end": v(-25.25, 10) * mm});
            skLineSegment(sketch, "E8.0.3.48", {"start": v(-47.25, 10) * mm, "end": v(-56.25, 10) * mm});
            skLineSegment(sketch, "E8.0.3.49", {"start": v(7.75, 19) * mm, "end": v(7.75, 10) * mm});
            skLineSegment(sketch, "E8.0.3.50", {"start": v(-24.25, 20) * mm, "end": v(-13.25, 20) * mm});
            skLineSegment(sketch, "E8.0.3.51", {"start": v(-35.25, 9) * mm, "end": v(-24.25, 9) * mm});
            skLineSegment(sketch, "E8.0.3.52", {"start": v(-23.25, 10) * mm, "end": v(-23.25, 19) * mm});
            skLineSegment(sketch, "E8.0.3.53", {"start": v(-3.25, 10) * mm, "end": v(-12.25, 10) * mm});
            skLineSegment(sketch, "E8.0.3.54", {"start": v(9.75, 10) * mm, "end": v(9.75, 19) * mm});
            skLineSegment(sketch, "E8.0.3.55", {"start": v(9.75, 19) * mm, "end": v(18.75, 19) * mm});
            skLineSegment(sketch, "E8.0.3.56", {"start": v(-23.25, 19) * mm, "end": v(-14.25, 19) * mm});
            skLineSegment(sketch, "E8.0.3.57", {"start": v(-2.25, 20) * mm, "end": v(8.75, 20) * mm, "construction": true});
            skLineSegment(sketch, "E8.0.3.58", {"start": v(-2.25, 20) * mm, "end": v(-2.25, 9) * mm});
            skLineSegment(sketch, "E8.0.3.59", {"start": v(8.75, 20) * mm, "end": v(19.75, 20) * mm, "construction": true});
            skLineSegment(sketch, "E8.0.3.60", {"start": v(19.75, 9) * mm, "end": v(19.75, 20) * mm, "construction": true});
            skLineSegment(sketch, "E8.0.3.61", {"start": v(-35.25, 20) * mm, "end": v(-35.25, 9) * mm});
            skLineSegment(sketch, "E8.0.3.62", {"start": v(-24.25, 20) * mm, "end": v(-13.25, 20) * mm, "construction": true});
            skLineSegment(sketch, "E8.0.3.63", {"start": v(-68.25, 20) * mm, "end": v(-57.25, 20) * mm, "construction": true});
            skLineSegment(sketch, "E8.0.3.64", {"start": v(-68.25, 9) * mm, "end": v(-57.25, 9) * mm, "construction": true});
            skLineSegment(sketch, "E8.0.3.65", {"start": v(-68.25, 9) * mm, "end": v(19.75, 9) * mm, "construction": true});
            skLineSegment(sketch, "E8.0.3.66", {"start": v(-35.25, 20) * mm, "end": v(-24.25, 20) * mm, "construction": true});
            skLineSegment(sketch, "E8.0.3.67", {"start": v(-57.25, 20) * mm, "end": v(-46.25, 20) * mm, "construction": true});
            skLineSegment(sketch, "E8.0.3.68", {"start": v(-13.25, 20) * mm, "end": v(-13.25, 9) * mm});
            skLineSegment(sketch, "E8.0.3.69", {"start": v(-46.25, 20) * mm, "end": v(-35.25, 20) * mm, "construction": true});
            skLineSegment(sketch, "E8.0.3.70", {"start": v(-13.25, 20) * mm, "end": v(-2.25, 20) * mm, "construction": true});
            skLineSegment(sketch, "E8.0.3.71", {"start": v(-24.25, 20) * mm, "end": v(-24.25, 9) * mm});
            skLineSegment(sketch, "E8.0.3.72", {"start": v(8.75, 20) * mm, "end": v(8.75, 9) * mm});
            skLineSegment(sketch, "E8.0.3.73", {"start": v(-46.25, 9) * mm, "end": v(-35.25, 9) * mm, "construction": true});
            skLineSegment(sketch, "E8.0.3.74", {"start": v(-46.25, 20) * mm, "end": v(-46.25, 9) * mm});
            skLineSegment(sketch, "E8.0.3.75", {"start": v(-57.25, 20) * mm, "end": v(-57.25, 9) * mm});
            skLineSegment(sketch, "E8.0.3.76", {"start": v(-2.25, 9) * mm, "end": v(8.75, 9) * mm, "construction": true});
            skLineSegment(sketch, "E8.0.3.77", {"start": v(-68.25, 9) * mm, "end": v(-57.25, 9) * mm, "construction": true});
            skLineSegment(sketch, "E8.0.3.78", {"start": v(-35.25, 9) * mm, "end": v(-24.25, 9) * mm, "construction": true});
            skLineSegment(sketch, "E8.0.3.79", {"start": v(-57.25, 9) * mm, "end": v(-57.25, 20) * mm, "construction": true});
            skLineSegment(sketch, "E8.0.3.80", {"start": v(8.75, 9) * mm, "end": v(8.75, 20) * mm, "construction": true});
            skLineSegment(sketch, "E8.0.3.81", {"start": v(8.75, 9) * mm, "end": v(19.75, 9) * mm, "construction": true});
            skLineSegment(sketch, "E8.0.3.82", {"start": v(-13.25, 9) * mm, "end": v(-13.25, 20) * mm, "construction": true});
            skLineSegment(sketch, "E8.0.3.83", {"start": v(-24.25, 9) * mm, "end": v(-24.25, 20) * mm, "construction": true});
            skLineSegment(sketch, "E8.0.3.84", {"start": v(-46.25, 9) * mm, "end": v(-46.25, 20) * mm, "construction": true});
            skLineSegment(sketch, "E8.0.3.85", {"start": v(-24.25, 9) * mm, "end": v(-13.25, 9) * mm, "construction": true});
            skLineSegment(sketch, "E8.0.3.86", {"start": v(-57.25, 9) * mm, "end": v(-46.25, 9) * mm, "construction": true});
            skLineSegment(sketch, "E8.0.3.87", {"start": v(-13.25, 9) * mm, "end": v(-2.25, 9) * mm, "construction": true});
            skLineSegment(sketch, "E8.0.3.88", {"start": v(-2.25, 9) * mm, "end": v(-2.25, 20) * mm, "construction": true});
            skLineSegment(sketch, "E8.0.3.89", {"start": v(-35.25, 9) * mm, "end": v(-35.25, 20) * mm, "construction": true});
            skLineSegment(sketch, "E8.0.4.0", {"start": v(-56.25, 21) * mm, "end": v(-56.25, 30) * mm});
            skLineSegment(sketch, "E8.0.4.1", {"start": v(-46.25, 31) * mm, "end": v(-35.25, 31) * mm});
            skLineSegment(sketch, "E8.0.4.2", {"start": v(-14.25, 30) * mm, "end": v(-14.25, 21) * mm});
            skLineSegment(sketch, "E8.0.4.3", {"start": v(-13.25, 31) * mm, "end": v(-13.25, 20) * mm});
            skLineSegment(sketch, "E8.0.4.4", {"start": v(-57.25, 20) * mm, "end": v(-46.25, 20) * mm});
            skLineSegment(sketch, "E8.0.4.5", {"start": v(-2.25, 31) * mm, "end": v(8.75, 31) * mm});
            skLineSegment(sketch, "E8.0.4.6", {"start": v(-45.25, 21) * mm, "end": v(-45.25, 30) * mm});
            skLineSegment(sketch, "E8.0.4.7", {"start": v(-25.25, 21) * mm, "end": v(-34.25, 21) * mm});
            skLineSegment(sketch, "E8.0.4.8", {"start": v(-13.25, 20) * mm, "end": v(-2.25, 20) * mm});
            skLineSegment(sketch, "E8.0.4.9", {"start": v(-45.25, 30) * mm, "end": v(-36.25, 30) * mm});
            skLineSegment(sketch, "E8.0.4.10", {"start": v(-58.25, 30) * mm, "end": v(-58.25, 21) * mm});
            skLineSegment(sketch, "E8.0.4.11", {"start": v(-12.25, 21) * mm, "end": v(-12.25, 30) * mm});
            skLineSegment(sketch, "E8.0.4.12", {"start": v(-67.25, 30) * mm, "end": v(-58.25, 30) * mm});
            skLineSegment(sketch, "E8.0.4.13", {"start": v(-57.25, 31) * mm, "end": v(-57.25, 20) * mm});
            skLineSegment(sketch, "E8.0.4.14", {"start": v(-68.25, 31) * mm, "end": v(-68.25, 20) * mm});
            skLineSegment(sketch, "E8.0.4.15", {"start": v(-68.25, 20) * mm, "end": v(-57.25, 20) * mm});
            skLineSegment(sketch, "E8.0.4.16", {"start": v(7.75, 21) * mm, "end": v(-1.25, 21) * mm});
            skLineSegment(sketch, "E8.0.4.17", {"start": v(-46.25, 20) * mm, "end": v(-35.25, 20) * mm});
            skLineSegment(sketch, "E8.0.4.18", {"start": v(-35.25, 31) * mm, "end": v(-24.25, 31) * mm});
            skLineSegment(sketch, "E8.0.4.19", {"start": v(-3.25, 30) * mm, "end": v(-3.25, 21) * mm});
            skLineSegment(sketch, "E8.0.4.20", {"start": v(8.75, 31) * mm, "end": v(8.75, 20) * mm});
            skLineSegment(sketch, "E8.0.4.21", {"start": v(-36.25, 30) * mm, "end": v(-36.25, 21) * mm});
            skLineSegment(sketch, "E8.0.4.22", {"start": v(-68.25, 31) * mm, "end": v(-57.25, 31) * mm});
            skLineSegment(sketch, "E8.0.4.23", {"start": v(-47.25, 30) * mm, "end": v(-47.25, 21) * mm});
            skLineSegment(sketch, "E8.0.4.24", {"start": v(-67.25, 21) * mm, "end": v(-67.25, 30) * mm});
            skLineSegment(sketch, "E8.0.4.25", {"start": v(-58.25, 21) * mm, "end": v(-67.25, 21) * mm});
            skLineSegment(sketch, "E8.0.4.26", {"start": v(-46.25, 31) * mm, "end": v(-46.25, 20) * mm});
            skLineSegment(sketch, "E8.0.4.27", {"start": v(-2.25, 31) * mm, "end": v(-2.25, 20) * mm});
            skLineSegment(sketch, "E8.0.4.28", {"start": v(-1.25, 30) * mm, "end": v(7.75, 30) * mm});
            skLineSegment(sketch, "E8.0.4.29", {"start": v(-24.25, 31) * mm, "end": v(-24.25, 20) * mm});
            skLineSegment(sketch, "E8.0.4.30", {"start": v(-35.25, 31) * mm, "end": v(-35.25, 20) * mm});
            skLineSegment(sketch, "E8.0.4.31", {"start": v(-12.25, 30) * mm, "end": v(-3.25, 30) * mm});
            skLineSegment(sketch, "E8.0.4.32", {"start": v(-1.25, 21) * mm, "end": v(-1.25, 30) * mm});
            skLineSegment(sketch, "E8.0.4.33", {"start": v(18.75, 21) * mm, "end": v(9.75, 21) * mm});
            skLineSegment(sketch, "E8.0.4.34", {"start": v(-34.25, 30) * mm, "end": v(-25.25, 30) * mm});
            skLineSegment(sketch, "E8.0.4.35", {"start": v(18.75, 30) * mm, "end": v(18.75, 21) * mm});
            skLineSegment(sketch, "E8.0.4.36", {"start": v(-13.25, 31) * mm, "end": v(-2.25, 31) * mm});
            skLineSegment(sketch, "E8.0.4.37", {"start": v(-24.25, 20) * mm, "end": v(-13.25, 20) * mm});
            skLineSegment(sketch, "E8.0.4.38", {"start": v(-36.25, 21) * mm, "end": v(-45.25, 21) * mm});
            skLineSegment(sketch, "E8.0.4.39", {"start": v(-2.25, 20) * mm, "end": v(8.75, 20) * mm});
            skLineSegment(sketch, "E8.0.4.40", {"start": v(8.75, 31) * mm, "end": v(19.75, 31) * mm});
            skLineSegment(sketch, "E8.0.4.41", {"start": v(-56.25, 30) * mm, "end": v(-47.25, 30) * mm});
            skLineSegment(sketch, "E8.0.4.42", {"start": v(8.75, 20) * mm, "end": v(19.75, 20) * mm});
            skLineSegment(sketch, "E8.0.4.43", {"start": v(-34.25, 21) * mm, "end": v(-34.25, 30) * mm});
            skLineSegment(sketch, "E8.0.4.44", {"start": v(-14.25, 21) * mm, "end": v(-23.25, 21) * mm});
            skLineSegment(sketch, "E8.0.4.45", {"start": v(-57.25, 31) * mm, "end": v(-46.25, 31) * mm});
            skLineSegment(sketch, "E8.0.4.46", {"start": v(19.75, 31) * mm, "end": v(19.75, 20) * mm});
            skLineSegment(sketch, "E8.0.4.47", {"start": v(-25.25, 30) * mm, "end": v(-25.25, 21) * mm});
            skLineSegment(sketch, "E8.0.4.48", {"start": v(-47.25, 21) * mm, "end": v(-56.25, 21) * mm});
            skLineSegment(sketch, "E8.0.4.49", {"start": v(7.75, 30) * mm, "end": v(7.75, 21) * mm});
            skLineSegment(sketch, "E8.0.4.50", {"start": v(-24.25, 31) * mm, "end": v(-13.25, 31) * mm});
            skLineSegment(sketch, "E8.0.4.51", {"start": v(-35.25, 20) * mm, "end": v(-24.25, 20) * mm});
            skLineSegment(sketch, "E8.0.4.52", {"start": v(-23.25, 21) * mm, "end": v(-23.25, 30) * mm});
            skLineSegment(sketch, "E8.0.4.53", {"start": v(-3.25, 21) * mm, "end": v(-12.25, 21) * mm});
            skLineSegment(sketch, "E8.0.4.54", {"start": v(9.75, 21) * mm, "end": v(9.75, 30) * mm});
            skLineSegment(sketch, "E8.0.4.55", {"start": v(9.75, 30) * mm, "end": v(18.75, 30) * mm});
            skLineSegment(sketch, "E8.0.4.56", {"start": v(-23.25, 30) * mm, "end": v(-14.25, 30) * mm});
            skLineSegment(sketch, "E8.0.4.57", {"start": v(-2.25, 31) * mm, "end": v(8.75, 31) * mm, "construction": true});
            skLineSegment(sketch, "E8.0.4.58", {"start": v(-2.25, 31) * mm, "end": v(-2.25, 20) * mm});
            skLineSegment(sketch, "E8.0.4.59", {"start": v(8.75, 31) * mm, "end": v(19.75, 31) * mm, "construction": true});
            skLineSegment(sketch, "E8.0.4.60", {"start": v(19.75, 20) * mm, "end": v(19.75, 31) * mm, "construction": true});
            skLineSegment(sketch, "E8.0.4.61", {"start": v(-35.25, 31) * mm, "end": v(-35.25, 20) * mm});
            skLineSegment(sketch, "E8.0.4.62", {"start": v(-24.25, 31) * mm, "end": v(-13.25, 31) * mm, "construction": true});
            skLineSegment(sketch, "E8.0.4.63", {"start": v(-68.25, 31) * mm, "end": v(-57.25, 31) * mm, "construction": true});
            skLineSegment(sketch, "E8.0.4.64", {"start": v(-68.25, 20) * mm, "end": v(-57.25, 20) * mm, "construction": true});
            skLineSegment(sketch, "E8.0.4.65", {"start": v(-68.25, 20) * mm, "end": v(19.75, 20) * mm, "construction": true});
            skLineSegment(sketch, "E8.0.4.66", {"start": v(-35.25, 31) * mm, "end": v(-24.25, 31) * mm, "construction": true});
            skLineSegment(sketch, "E8.0.4.67", {"start": v(-57.25, 31) * mm, "end": v(-46.25, 31) * mm, "construction": true});
            skLineSegment(sketch, "E8.0.4.68", {"start": v(-13.25, 31) * mm, "end": v(-13.25, 20) * mm});
            skLineSegment(sketch, "E8.0.4.69", {"start": v(-46.25, 31) * mm, "end": v(-35.25, 31) * mm, "construction": true});
            skLineSegment(sketch, "E8.0.4.70", {"start": v(-13.25, 31) * mm, "end": v(-2.25, 31) * mm, "construction": true});
            skLineSegment(sketch, "E8.0.4.71", {"start": v(-24.25, 31) * mm, "end": v(-24.25, 20) * mm});
            skLineSegment(sketch, "E8.0.4.72", {"start": v(8.75, 31) * mm, "end": v(8.75, 20) * mm});
            skLineSegment(sketch, "E8.0.4.73", {"start": v(-46.25, 20) * mm, "end": v(-35.25, 20) * mm, "construction": true});
            skLineSegment(sketch, "E8.0.4.74", {"start": v(-46.25, 31) * mm, "end": v(-46.25, 20) * mm});
            skLineSegment(sketch, "E8.0.4.75", {"start": v(-57.25, 31) * mm, "end": v(-57.25, 20) * mm});
            skLineSegment(sketch, "E8.0.4.76", {"start": v(-2.25, 20) * mm, "end": v(8.75, 20) * mm, "construction": true});
            skLineSegment(sketch, "E8.0.4.77", {"start": v(-68.25, 20) * mm, "end": v(-57.25, 20) * mm, "construction": true});
            skLineSegment(sketch, "E8.0.4.78", {"start": v(-35.25, 20) * mm, "end": v(-24.25, 20) * mm, "construction": true});
            skLineSegment(sketch, "E8.0.4.79", {"start": v(-57.25, 20) * mm, "end": v(-57.25, 31) * mm, "construction": true});
            skLineSegment(sketch, "E8.0.4.80", {"start": v(8.75, 20) * mm, "end": v(8.75, 31) * mm, "construction": true});
            skLineSegment(sketch, "E8.0.4.81", {"start": v(8.75, 20) * mm, "end": v(19.75, 20) * mm, "construction": true});
            skLineSegment(sketch, "E8.0.4.82", {"start": v(-13.25, 20) * mm, "end": v(-13.25, 31) * mm, "construction": true});
            skLineSegment(sketch, "E8.0.4.83", {"start": v(-24.25, 20) * mm, "end": v(-24.25, 31) * mm, "construction": true});
            skLineSegment(sketch, "E8.0.4.84", {"start": v(-46.25, 20) * mm, "end": v(-46.25, 31) * mm, "construction": true});
            skLineSegment(sketch, "E8.0.4.85", {"start": v(-24.25, 20) * mm, "end": v(-13.25, 20) * mm, "construction": true});
            skLineSegment(sketch, "E8.0.4.86", {"start": v(-57.25, 20) * mm, "end": v(-46.25, 20) * mm, "construction": true});
            skLineSegment(sketch, "E8.0.4.87", {"start": v(-13.25, 20) * mm, "end": v(-2.25, 20) * mm, "construction": true});
            skLineSegment(sketch, "E8.0.4.88", {"start": v(-2.25, 20) * mm, "end": v(-2.25, 31) * mm, "construction": true});
            skLineSegment(sketch, "E8.0.4.89", {"start": v(-35.25, 20) * mm, "end": v(-35.25, 31) * mm, "construction": true});
            skLineSegment(sketch, "E8.direction1", {"start": v(-68.25, -24) * mm, "end": v(-43.25, -24) * mm, "construction": true});
            skLineSegment(sketch, "E8.direction2", {"start": v(-68.25, -24) * mm, "end": v(-68.25, -13) * mm, "construction": true});
            skSolve(sketch);
        }
        {
            var Q0;
            Q0=makeQuery(id+"F0.imprint","IMPRINT",FACE,{"disambiguationData":[TD([[makeQuery(id+"F0.imprint","IMPRINT",EDGE,{"derivedFrom":sQuery(id+"F0.wireOp",EDGE,"E8.0.2.7")}),1.0]])]});
            var Q1;
            Q1=makeQuery(id+"F0.imprint","IMPRINT",FACE,{"disambiguationData":[TD([[makeQuery(id+"F0.imprint","IMPRINT",EDGE,{"derivedFrom":sQuery(id+"F0.wireOp",EDGE,"E8.0.2.6")}),1.0]])]});
            var Q2;
            Q2=makeQuery(id+"F0.imprint","IMPRINT",FACE,{"disambiguationData":[TD([[makeQuery(id+"F0.imprint","IMPRINT",EDGE,{"derivedFrom":sQuery(id+"F0.wireOp",EDGE,"E8.0.2.0")}),1.0]])]});
            var Q3;
            Q3=makeQuery(id+"F0.imprint","IMPRINT",FACE,{"disambiguationData":[TD([[makeQuery(id+"F0.imprint","IMPRINT",EDGE,{"derivedFrom":sQuery(id+"F0.wireOp",EDGE,"E8.0.2.10")}),1.0]])]});
            var Q4;
            Q4=makeQuery(id+"F0.imprint","IMPRINT",FACE,{"disambiguationData":[TD([[makeQuery(id+"F0.imprint","IMPRINT",EDGE,{"derivedFrom":sQuery(id+"F0.wireOp",EDGE,"E8.0.1.0")}),1.0]])]});
            var Q5;
            Q5=makeQuery(id+"F0.imprint","IMPRINT",FACE,{"disambiguationData":[TD([[makeQuery(id+"F0.imprint","IMPRINT",EDGE,{"derivedFrom":sQuery(id+"F0.wireOp",EDGE,"E8.0.1.10")}),1.0]])]});
            var Q6;
            Q6=makeQuery(id+"F0.imprint","IMPRINT",FACE,{"disambiguationData":[TD([[makeQuery(id+"F0.imprint","IMPRINT",EDGE,{"derivedFrom":sQuery(id+"F0.wireOp",EDGE,"E2.top")}),1.0]])]});
            var Q7;
            Q7=makeQuery(id+"F0.imprint","IMPRINT",FACE,{"disambiguationData":[TD([[makeQuery(id+"F0.imprint","IMPRINT",EDGE,{"derivedFrom":sQuery(id+"F0.wireOp",EDGE,"E7.1.0.0")}),1.0]])]});
            var Q8;
            Q8=makeQuery(id+"F0.imprint","IMPRINT",FACE,{"disambiguationData":[TD([[makeQuery(id+"F0.imprint","IMPRINT",EDGE,{"derivedFrom":sQuery(id+"F0.wireOp",EDGE,"E8.0.1.6")}),1.0]])]});
            var Q9;
            Q9=makeQuery(id+"F0.imprint","IMPRINT",FACE,{"disambiguationData":[TD([[makeQuery(id+"F0.imprint","IMPRINT",EDGE,{"derivedFrom":sQuery(id+"F0.wireOp",EDGE,"E7.2.0.0")}),1.0]])]});
            var Q10;
            Q10=makeQuery(id+"F0.imprint","IMPRINT",FACE,{"disambiguationData":[TD([[makeQuery(id+"F0.imprint","IMPRINT",EDGE,{"derivedFrom":sQuery(id+"F0.wireOp",EDGE,"E7.3.0.0")}),1.0]])]});
            var Q11;
            Q11=makeQuery(id+"F0.imprint","IMPRINT",FACE,{"disambiguationData":[TD([[makeQuery(id+"F0.imprint","IMPRINT",EDGE,{"derivedFrom":sQuery(id+"F0.wireOp",EDGE,"E8.0.1.7")}),1.0]])]});
            var Q12;
            Q12=makeQuery(id+"F0.imprint","IMPRINT",FACE,{"disambiguationData":[TD([[makeQuery(id+"F0.imprint","IMPRINT",EDGE,{"derivedFrom":sQuery(id+"F0.wireOp",EDGE,"E8.0.1.2")}),1.0]])]});
            var Q13;
            Q13=makeQuery(id+"F0.imprint","IMPRINT",FACE,{"disambiguationData":[TD([[makeQuery(id+"F0.imprint","IMPRINT",EDGE,{"derivedFrom":sQuery(id+"F0.wireOp",EDGE,"E8.0.2.2")}),1.0]])]});
            var Q14;
            Q14=makeQuery(id+"F0.imprint","IMPRINT",FACE,{"disambiguationData":[TD([[makeQuery(id+"F0.imprint","IMPRINT",EDGE,{"derivedFrom":sQuery(id+"F0.wireOp",EDGE,"E7.4.0.0")}),1.0]])]});
            var Q15;
            Q15=makeQuery(id+"F0.imprint","IMPRINT",FACE,{"disambiguationData":[TD([[makeQuery(id+"F0.imprint","IMPRINT",EDGE,{"derivedFrom":sQuery(id+"F0.wireOp",EDGE,"E7.5.0.0")}),1.0]])]});
            var Q16;
            Q16=makeQuery(id+"F0.imprint","IMPRINT",FACE,{"disambiguationData":[TD([[makeQuery(id+"F0.imprint","IMPRINT",EDGE,{"derivedFrom":sQuery(id+"F0.wireOp",EDGE,"E7.5.0.6")}),1.0]])]});
            var Q17;
            Q17=makeQuery(id+"F0.imprint","IMPRINT",FACE,{"disambiguationData":[TD([[makeQuery(id+"F0.imprint","IMPRINT",EDGE,{"derivedFrom":sQuery(id+"F0.wireOp",EDGE,"E8.0.1.16")}),1.0]])]});
            var Q18;
            Q18=makeQuery(id+"F0.imprint","IMPRINT",FACE,{"disambiguationData":[TD([[makeQuery(id+"F0.imprint","IMPRINT",EDGE,{"derivedFrom":sQuery(id+"F0.wireOp",EDGE,"E7.6.0.0")}),1.0]])]});
            var Q19;
            Q19=makeQuery(id+"F0.imprint","IMPRINT",FACE,{"disambiguationData":[TD([[makeQuery(id+"F0.imprint","IMPRINT",EDGE,{"derivedFrom":sQuery(id+"F0.wireOp",EDGE,"E7.7.0.0")}),1.0]])]});
            var Q20;
            Q20=makeQuery(id+"F0.imprint","IMPRINT",FACE,{"disambiguationData":[TD([[makeQuery(id+"F0.imprint","IMPRINT",EDGE,{"derivedFrom":sQuery(id+"F0.wireOp",EDGE,"E8.0.1.33")}),1.0]])]});
            var Q21;
            Q21=makeQuery(id+"F0.imprint","IMPRINT",FACE,{"disambiguationData":[TD([[makeQuery(id+"F0.imprint","IMPRINT",EDGE,{"derivedFrom":sQuery(id+"F0.wireOp",EDGE,"E8.0.2.33")}),1.0]])]});
            var Q22;
            Q22=makeQuery(id+"F0.imprint","IMPRINT",FACE,{"disambiguationData":[TD([[makeQuery(id+"F0.imprint","IMPRINT",EDGE,{"derivedFrom":sQuery(id+"F0.wireOp",EDGE,"E8.0.2.16")}),1.0]])]});
            var Q23;
            Q23=makeQuery(id+"F0.imprint","IMPRINT",FACE,{"disambiguationData":[TD([[makeQuery(id+"F0.imprint","IMPRINT",EDGE,{"derivedFrom":sQuery(id+"F0.wireOp",EDGE,"E8.0.2.8")}),1.0]])]});
            var Q24;
            Q24=makeQuery(id+"F0.imprint","IMPRINT",FACE,{"disambiguationData":[TD([[makeQuery(id+"F0.imprint","IMPRINT",EDGE,{"derivedFrom":sQuery(id+"F0.wireOp",EDGE,"E8.0.3.33")}),1.0]])]});
            var Q25;
            Q25=makeQuery(id+"F0.imprint","IMPRINT",FACE,{"disambiguationData":[TD([[makeQuery(id+"F0.imprint","IMPRINT",EDGE,{"derivedFrom":sQuery(id+"F0.wireOp",EDGE,"E8.0.3.16")}),1.0]])]});
            var Q26;
            Q26=makeQuery(id+"F0.imprint","IMPRINT",FACE,{"disambiguationData":[TD([[makeQuery(id+"F0.imprint","IMPRINT",EDGE,{"derivedFrom":sQuery(id+"F0.wireOp",EDGE,"E8.0.3.8")}),1.0]])]});
            var Q27;
            Q27=makeQuery(id+"F0.imprint","IMPRINT",FACE,{"disambiguationData":[TD([[makeQuery(id+"F0.imprint","IMPRINT",EDGE,{"derivedFrom":sQuery(id+"F0.wireOp",EDGE,"E8.0.4.33")}),1.0]])]});
            var Q28;
            Q28=makeQuery(id+"F0.imprint","IMPRINT",FACE,{"disambiguationData":[TD([[makeQuery(id+"F0.imprint","IMPRINT",EDGE,{"derivedFrom":sQuery(id+"F0.wireOp",EDGE,"E8.0.4.5")}),-1.0]])]});
            var Q29;
            Q29=makeQuery(id+"F0.imprint","IMPRINT",FACE,{"disambiguationData":[TD([[makeQuery(id+"F0.imprint","IMPRINT",EDGE,{"derivedFrom":sQuery(id+"F0.wireOp",EDGE,"E8.0.3.2")}),1.0]])]});
            var Q30;
            Q30=makeQuery(id+"F0.imprint","IMPRINT",FACE,{"disambiguationData":[TD([[makeQuery(id+"F0.imprint","IMPRINT",EDGE,{"derivedFrom":sQuery(id+"F0.wireOp",EDGE,"E8.0.4.8")}),1.0]])]});
            var Q31;
            Q31=makeQuery(id+"F0.imprint","IMPRINT",FACE,{"disambiguationData":[TD([[makeQuery(id+"F0.imprint","IMPRINT",EDGE,{"derivedFrom":sQuery(id+"F0.wireOp",EDGE,"E8.0.4.2")}),1.0]])]});
            var Q32;
            Q32=makeQuery(id+"F0.imprint","IMPRINT",FACE,{"disambiguationData":[TD([[makeQuery(id+"F0.imprint","IMPRINT",EDGE,{"derivedFrom":sQuery(id+"F0.wireOp",EDGE,"E8.0.3.7")}),1.0]])]});
            var Q33;
            Q33=makeQuery(id+"F0.imprint","IMPRINT",FACE,{"disambiguationData":[TD([[makeQuery(id+"F0.imprint","IMPRINT",EDGE,{"derivedFrom":sQuery(id+"F0.wireOp",EDGE,"E8.0.4.7")}),1.0]])]});
            var Q34;
            Q34=makeQuery(id+"F0.imprint","IMPRINT",FACE,{"disambiguationData":[TD([[makeQuery(id+"F0.imprint","IMPRINT",EDGE,{"derivedFrom":sQuery(id+"F0.wireOp",EDGE,"E8.0.3.6")}),1.0]])]});
            var Q35;
            Q35=makeQuery(id+"F0.imprint","IMPRINT",FACE,{"disambiguationData":[TD([[makeQuery(id+"F0.imprint","IMPRINT",EDGE,{"derivedFrom":sQuery(id+"F0.wireOp",EDGE,"E8.0.4.1")}),-1.0]])]});
            var Q36;
            Q36=makeQuery(id+"F0.imprint","IMPRINT",FACE,{"disambiguationData":[TD([[makeQuery(id+"F0.imprint","IMPRINT",EDGE,{"derivedFrom":sQuery(id+"F0.wireOp",EDGE,"E8.0.3.0")}),1.0]])]});
            var Q37;
            Q37=makeQuery(id+"F0.imprint","IMPRINT",FACE,{"disambiguationData":[TD([[makeQuery(id+"F0.imprint","IMPRINT",EDGE,{"derivedFrom":sQuery(id+"F0.wireOp",EDGE,"E8.0.4.0")}),1.0]])]});
            var Q38;
            Q38=makeQuery(id+"F0.imprint","IMPRINT",FACE,{"disambiguationData":[TD([[makeQuery(id+"F0.imprint","IMPRINT",EDGE,{"derivedFrom":sQuery(id+"F0.wireOp",EDGE,"E8.0.3.10")}),1.0]])]});
            var Q39;
            Q39=makeQuery(id+"F0.imprint","IMPRINT",FACE,{"disambiguationData":[TD([[makeQuery(id+"F0.imprint","IMPRINT",EDGE,{"derivedFrom":sQuery(id+"F0.wireOp",EDGE,"E8.0.4.10")}),1.0]])]});
            extrude(context, id + "F1", {"entities" : qUnion([Q0, Q1, Q2, Q3, Q4, Q5, Q6, Q7, Q8, Q9, Q10, Q11, Q12, Q13, Q14, Q15, Q16, Q17, Q18, Q19, Q20, Q21, Q22, Q23, Q24, Q25, Q26, Q27, Q28, Q29, Q30, Q31, Q32, Q33, Q34, Q35, Q36, Q37, Q38, Q39]), "depth" : 1.5 * mm});
        }
        {
            var Q0;
            Q0=qCreatedBy(makeId("Top.planeOp"),FACE);
            cPlane(context, id + "F2", {"entities" : qUnion([Q0]), "cplaneType" : CPlaneType.OFFSET, "offset" : 2 * mm, "width" : 150 * mm, "height" : 150 * mm});
        }
    });
